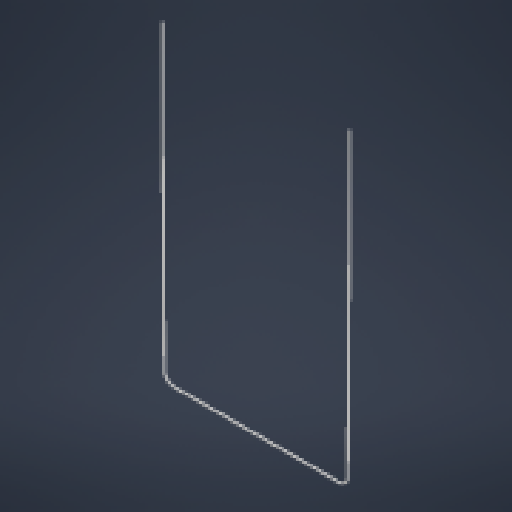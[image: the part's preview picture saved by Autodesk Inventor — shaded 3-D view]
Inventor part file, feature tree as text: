
AUTODESK INVENTOR PART (.ipt)
format: ipt  version: 2024 (Build 280153000, 153)  size: 216,576 bytes
history: native  units: in
note: dims shown in document units (in); Inventor stores cm internally (conversion verified against a paired STEP export)
features: sketch x2, plane x1, sweep x1
ambient origin geometry x8: Origin, YZ Plane, XZ Plane, XY Plane, X Axis, Y Axis, Z Axis, Center Point
bodies: Body1 (feature_tree)
feature tree (4):
  sketch  "Sketch3"  dims[d13=9.8in d18=0.5in]
  plane  "Work Plane2"
  sweep  "Sweep2"
  sketch  "Sketch4"  dims[d19=0.1181in d20=0.0in d21=0.0in d23=0.1in d24=0.1in d25=1.0in d26=1.0in]
